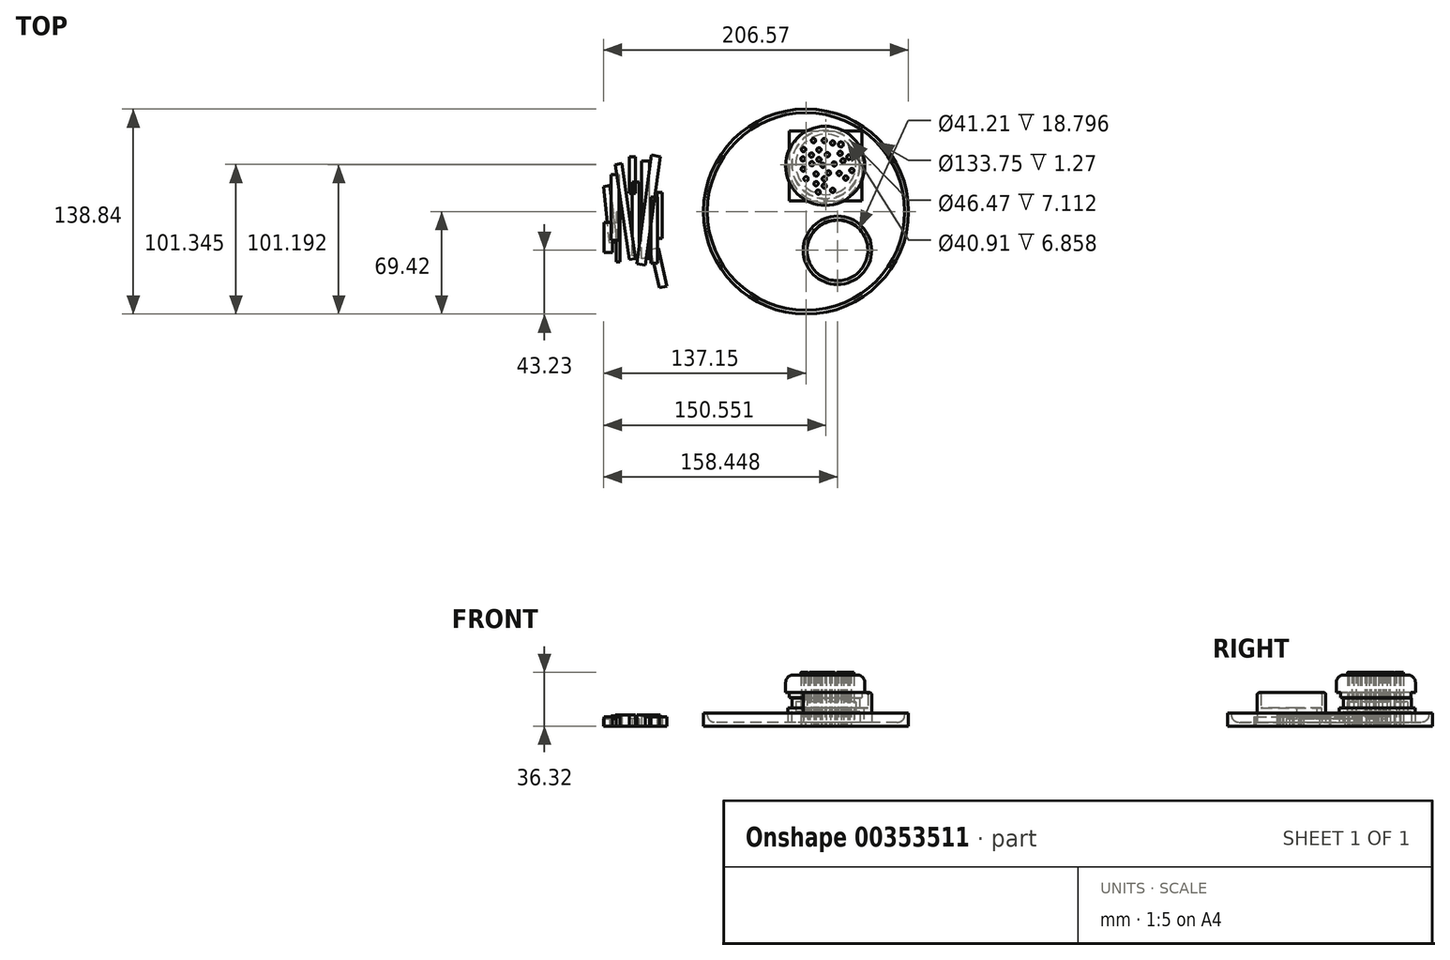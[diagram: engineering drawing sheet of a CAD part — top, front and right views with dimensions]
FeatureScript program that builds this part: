
annotation { "Feature Type Name" : "Feature", "Feature Type Description" : "" }
export const myFeature = defineFeature(function(context is Context, id is Id, definition is map)
    precondition{}
    {
        {
            var Q0;
            Q0=qCreatedBy(makeId("Top.planeOp"),FACE);
            var sketch = newSketch(context, id + "F0", { "sketchPlane" : qUnion([Q0])});
            skCircle(sketch, "E0", {"center": v(0, 0) * mm, "radius": 69.42 * mm});
            skSolve(sketch);
        }
        {
            var Q0;
            Q0=makeQuery(id+"F0.imprint","IMPRINT",FACE,{"disambiguationData":[TD([[makeQuery(id+"F0.imprint","IMPRINT",EDGE,{"derivedFrom":sQuery(id+"F0.wireOp",EDGE,"E0")}),1.0]])]});
            extrude(context, id + "F1", {"entities" : qUnion([Q0]), "depth" : 8.9 * mm});
        }
        {
            var Q0;
            Q0=makeQuery(id+"F1.opExtrude","CAP_FACE",FACE,{"disambiguationData":[OSD([sQuery(id+"F0.wireOp",EDGE,"E0")])],"isStart":false});
            shell(context, id + "F2", {"entities" : qUnion([Q0]), "thickness" : 2.54 * mm});
        }
        {
            var Q0;
            {var subQ0=sQuery(id+"F0.wireOp",EDGE,"E0");Q0=makeQuery(id+"F2.opShell","OFFSET_FACE",FACE,{"disambiguationData":[OSD([subQ0]),TDD([makeQuery(id+"F1.opExtrude","CAP_FACE",FACE,{"disambiguationData":[OSD([subQ0])],"isStart":true})])]});}
            fillet(context, id + "F3", {"entities" : qUnion([Q0]), "radius" : 5.08 * mm, "tangentPropagation" : true, "allowEdgeOverflow" : false});
        }
        {
            var Q0;
            Q0=qCreatedBy(makeId("Top.planeOp"),FACE);
            var sketch = newSketch(context, id + "F4", { "sketchPlane" : qUnion([Q0])});
            skCircle(sketch, "E1", {"center": v(13.4, 31.77) * mm, "radius": 25.78 * mm});
            skSolve(sketch);
        }
        {
            var Q0;
            Q0 = qSketchRegion(id + "F4", true);
            extrude(context, id + "F5", {"entities" : qUnion([Q0]), "operationType" : NewBodyOperationType.ADD, "depth" : 12.2 * mm});
        }
        {
            var Q0;
            Q0=qCreatedBy(makeId("Top.planeOp"),FACE);
            var sketch = newSketch(context, id + "F6", { "sketchPlane" : qUnion([Q0])});
            skCircle(sketch, "E2", {"center": v(13.4, 31.93) * mm, "radius": 23 * mm});
            skSolve(sketch);
        }
        {
            var Q0;
            Q0 = qSketchRegion(id + "F6", true);
            extrude(context, id + "F7", {"entities" : qUnion([Q0]), "operationType" : NewBodyOperationType.ADD, "depth" : 19.05 * mm});
        }
        {
            var Q0;
            Q0=qCreatedBy(makeId("Top.planeOp"),FACE);
            var sketch = newSketch(context, id + "F8", { "sketchPlane" : qUnion([Q0])});
            skLineSegment(sketch, "E3.bottom", {"start": v(-11.22, 54.68) * mm, "end": v(37.7, 54.68) * mm});
            skLineSegment(sketch, "E3.top", {"start": v(-11.22, 7.2) * mm, "end": v(37.7, 7.2) * mm});
            skLineSegment(sketch, "E3.left", {"start": v(-11.22, 54.68) * mm, "end": v(-11.22, 7.2) * mm});
            skLineSegment(sketch, "E3.right", {"start": v(37.7, 54.68) * mm, "end": v(37.7, 7.2) * mm});
            skSolve(sketch);
        }
        {
            var Q0;
            Q0 = qSketchRegion(id + "F8", true);
            extrude(context, id + "F9", {"entities" : qUnion([Q0]), "depth" : 22.86 * mm, "hasSecondDirection" : true, "secondDirectionOppositeDirection" : false, "secondDirectionDepth" : 19.3 * mm});
        }
        {
            var Q0;
            Q0=qCreatedBy(makeId("Top.planeOp"),FACE);
            var sketch = newSketch(context, id + "F10", { "sketchPlane" : qUnion([Q0])});
            skCircle(sketch, "E4", {"center": v(13, 30.94) * mm, "radius": 26.8 * mm});
            skSolve(sketch);
        }
        {
            var Q0;
            Q0 = qSketchRegion(id + "F10", true);
            extrude(context, id + "F11", {"entities" : qUnion([Q0]), "depth" : 34.54 * mm, "hasSecondDirection" : true, "secondDirectionOppositeDirection" : false, "secondDirectionDepth" : 22.6 * mm});
        }
        {
            var Q0;
            Q0=makeQuery(id+"F11.opExtrude","CAP_FACE",FACE,{"disambiguationData":[OSD([sQuery(id+"F10.wireOp",EDGE,"E4")])],"isStart":false});
            fillet(context, id + "F12", {"entities" : qUnion([Q0]), "radius" : 5.08 * mm, "tangentPropagation" : true, "allowEdgeOverflow" : false});
        }
        {
            var Q0;
            Q0=qCreatedBy(makeId("Top.planeOp"),FACE);
            var sketch = newSketch(context, id + "F13", { "sketchPlane" : qUnion([Q0])});
            skCircle(sketch, "E5", {"center": v(0, 22.16) * mm, "radius": 1.47 * mm});
            skCircle(sketch, "E6", {"center": v(12.38, 22.16) * mm, "radius": 1.44 * mm});
            skCircle(sketch, "E7.1.0", {"center": v(6.76, 25.4) * mm, "radius": 1.44 * mm});
            skCircle(sketch, "E7.2.0", {"center": v(6.76, 18.92) * mm, "radius": 1.44 * mm});
            skPoint(sketch, "E7.center", {"position": v(8.63, 22.16) * mm});
            skCircle(sketch, "E8.1.0", {"center": v(11.4, 31.35) * mm, "radius": 1.44 * mm});
            skCircle(sketch, "E8.2.0", {"center": v(3.93, 32.4) * mm, "radius": 1.44 * mm});
            skPoint(sketch, "E8.center", {"position": v(7.37, 29.72) * mm});
            skCircle(sketch, "E9.1.0", {"center": v(19.1, 32.28) * mm, "radius": 1.44 * mm});
            skCircle(sketch, "E9.2.0", {"center": v(14.45, 38.48) * mm, "radius": 1.44 * mm});
            skPoint(sketch, "E9.center", {"position": v(14.99, 34.04) * mm});
            skCircle(sketch, "E10.1.0", {"center": v(15.25, 26.2) * mm, "radius": 1.44 * mm});
            skCircle(sketch, "E10.2.0", {"center": v(22.45, 25.9) * mm, "radius": 1.44 * mm});
            skPoint(sketch, "E10.center", {"position": v(18.93, 28.12) * mm});
            skCircle(sketch, "E11.1.0", {"center": v(-2.09, 35.6) * mm, "radius": 1.44 * mm});
            skCircle(sketch, "E11.2.0", {"center": v(-1.84, 28.79) * mm, "radius": 1.44 * mm});
            skPoint(sketch, "E11.center", {"position": v(0, 32.26) * mm});
            skCircle(sketch, "E12.1.0", {"center": v(8.75, 41.77) * mm, "radius": 1.44 * mm});
            skCircle(sketch, "E12.2.0", {"center": v(8.75, 35.18) * mm, "radius": 1.44 * mm});
            skPoint(sketch, "E12.center", {"position": v(10.65, 38.48) * mm});
            skCircle(sketch, "E13.1.0", {"center": v(3.66, 38.31) * mm, "radius": 1.44 * mm});
            skCircle(sketch, "E13.2.0", {"center": v(-1.57, 41.92) * mm, "radius": 1.44 * mm});
            skPoint(sketch, "E13.center", {"position": v(0, 38.6) * mm});
            skCircle(sketch, "E14.1.0", {"center": v(18.05, 14.36) * mm, "radius": 1.44 * mm});
            skCircle(sketch, "E14.2.0", {"center": v(26.9, 22.7) * mm, "radius": 1.44 * mm});
            skPoint(sketch, "E14.center", {"position": v(20.07, 21.08) * mm});
            skCircle(sketch, "E15.1.0", {"center": v(8.25, 13.24) * mm, "radius": 1.44 * mm});
            skCircle(sketch, "E15.2.0", {"center": v(12.42, 17.37) * mm, "radius": 1.44 * mm});
            skPoint(sketch, "E15.center", {"position": v(9.14, 16.51) * mm});
            skCircle(sketch, "E16.1.0", {"center": v(12.38, 48.07) * mm, "radius": 1.44 * mm});
            skCircle(sketch, "E16.2.0", {"center": v(5.1, 48.07) * mm, "radius": 1.44 * mm});
            skPoint(sketch, "E16.center", {"position": v(8.75, 45.97) * mm});
            skCircle(sketch, "E17.1.0", {"center": v(23.12, 39.32) * mm, "radius": 1.44 * mm});
            skCircle(sketch, "E17.2.0", {"center": v(18.05, 46.4) * mm, "radius": 1.44 * mm});
            skPoint(sketch, "E17.center", {"position": v(18.54, 41.4) * mm});
            skCircle(sketch, "E18.1.0", {"center": v(31.05, 27.84) * mm, "radius": 1.44 * mm});
            skCircle(sketch, "E18.2.0", {"center": v(25.07, 34.32) * mm, "radius": 1.44 * mm});
            skPoint(sketch, "E18.center", {"position": v(26.2, 29.36) * mm});
            skCircle(sketch, "E19", {"center": v(23.6, 45.47) * mm, "radius": 1.68 * mm});
            skCircle(sketch, "E20", {"center": v(29.07, 36.84) * mm, "radius": 1.55 * mm});
            skSolve(sketch);
        }
        {
            var Q0;
            Q0 = qSketchRegion(id + "F13", true);
            extrude(context, id + "F14", {"entities" : qUnion([Q0]), "depth" : 36.32 * mm});
        }
        {
            var Q0;
            Q0=qCreatedBy(makeId("Top.planeOp"),FACE);
            var sketch = newSketch(context, id + "F15", { "sketchPlane" : qUnion([Q0])});
            skCircle(sketch, "E21", {"center": v(21.3, -26.2) * mm, "radius": 23.15 * mm});
            skSolve(sketch);
        }
        {
            var Q0;
            Q0 = qSketchRegion(id + "F15", true);
            extrude(context, id + "F16", {"entities" : qUnion([Q0]), "operationType" : NewBodyOperationType.ADD, "depth" : 22.6 * mm});
        }
        {
            var Q0;
            Q0=makeQuery(id+"F16.opExtrude","CAP_FACE",FACE,{"disambiguationData":[OSD([sQuery(id+"F15.wireOp",EDGE,"E21")])],"isStart":false});
            shell(context, id + "F17", {"entities" : qUnion([Q0]), "thickness" : 2.54 * mm});
        }
        {
            var Q0;
            Q0=qCreatedBy(makeId("Top.planeOp"),FACE);
            var sketch = newSketch(context, id + "F18", { "sketchPlane" : qUnion([Q0])});
            skCircle(sketch, "E22", {"center": v(21.59, -26.86) * mm, "radius": 21.01 * mm});
            skSolve(sketch);
        }
        {
            var Q0;
            Q0 = qSketchRegion(id + "F18", true);
            extrude(context, id + "F19", {"entities" : qUnion([Q0]), "operationType" : NewBodyOperationType.ADD, "depth" : 12.2 * mm});
        }
        {
            var Q0;
            Q0=makeQuery(id+"F16.opExtrude","CAP_FACE",FACE,{"disambiguationData":[OSD([sQuery(id+"F15.wireOp",EDGE,"E21")])],"isStart":false});
            fillet(context, id + "F20", {"entities" : qUnion([Q0]), "radius" : 1.27 * mm, "tangentPropagation" : true, "allowEdgeOverflow" : false});
        }
        {
            var Q0;
            {var subQ0=sQuery(id+"F0.wireOp",EDGE,"E0");Q0=makeQuery(id+"F2.opShell","OFFSET_FACE",FACE,{"disambiguationData":[OSD([subQ0]),TDD([makeQuery(id+"F1.opExtrude","CAP_FACE",FACE,{"disambiguationData":[OSD([subQ0])],"isStart":true})])]});}
            var sketch = newSketch(context, id + "F21", { "sketchPlane" : qUnion([Q0])});
            skLineSegment(sketch, "E23", {"start": v(-16.66, -51.58) * mm, "end": v(-11.5, -50.47) * mm});
            skLineSegment(sketch, "E24", {"start": v(-11.5, -50.47) * mm, "end": v(-17.03, -24.69) * mm});
            skLineSegment(sketch, "E25", {"start": v(-16.66, -51.58) * mm, "end": v(-22.18, -25.8) * mm});
            skLineSegment(sketch, "E26", {"start": v(-17.03, -24.69) * mm, "end": v(-22.18, -25.8) * mm});
            skLineSegment(sketch, "E27.bottom", {"start": v(-17.7, -35.04) * mm, "end": v(-22.38, -35.04) * mm});
            skLineSegment(sketch, "E27.top", {"start": v(-17.7, 9.94) * mm, "end": v(-22.38, 9.94) * mm});
            skLineSegment(sketch, "E27.left", {"start": v(-17.7, -35.04) * mm, "end": v(-17.7, 9.94) * mm});
            skLineSegment(sketch, "E27.right", {"start": v(-22.38, -35.04) * mm, "end": v(-22.38, 9.94) * mm});
            skLineSegment(sketch, "E28.bottom", {"start": v(-18.01, -18.14) * mm, "end": v(-14.48, -18.14) * mm});
            skLineSegment(sketch, "E28.top", {"start": v(-18.01, 12.94) * mm, "end": v(-14.48, 12.94) * mm});
            skLineSegment(sketch, "E28.left", {"start": v(-18.01, -18.14) * mm, "end": v(-18.01, 12.94) * mm});
            skLineSegment(sketch, "E28.right", {"start": v(-14.48, -18.14) * mm, "end": v(-14.48, 12.94) * mm});
            skLineSegment(sketch, "E29.bottom", {"start": v(-23.27, -31.75) * mm, "end": v(-28.7, -31.75) * mm});
            skLineSegment(sketch, "E29.top", {"start": v(-23.27, 34.38) * mm, "end": v(-28.7, 34.38) * mm});
            skLineSegment(sketch, "E29.left", {"start": v(-23.27, -31.75) * mm, "end": v(-23.27, 34.38) * mm});
            skLineSegment(sketch, "E29.right", {"start": v(-28.7, -31.75) * mm, "end": v(-28.7, 34.38) * mm});
            skLineSegment(sketch, "E30", {"start": v(-31.92, -35.38) * mm, "end": v(-25.96, -36.2) * mm});
            skLineSegment(sketch, "E31", {"start": v(-25.96, -36.2) * mm, "end": v(-15.94, 37.11) * mm});
            skLineSegment(sketch, "E32", {"start": v(-31.92, -35.38) * mm, "end": v(-21.85, 38.21) * mm});
            skLineSegment(sketch, "E33", {"start": v(-21.85, 38.21) * mm, "end": v(-15.94, 37.11) * mm});
            skLineSegment(sketch, "E34.bottom", {"start": v(-30.05, -29.87) * mm, "end": v(-34.83, -29.87) * mm});
            skLineSegment(sketch, "E34.top", {"start": v(-30.05, 19.9) * mm, "end": v(-34.83, 19.9) * mm});
            skLineSegment(sketch, "E34.left", {"start": v(-30.05, -29.87) * mm, "end": v(-30.05, 19.9) * mm});
            skLineSegment(sketch, "E34.right", {"start": v(-34.83, -29.87) * mm, "end": v(-34.83, 19.9) * mm});
            skLineSegment(sketch, "E35.bottom", {"start": v(-32.72, 12.42) * mm, "end": v(-36.92, 12.42) * mm});
            skLineSegment(sketch, "E35.top", {"start": v(-32.72, 37.2) * mm, "end": v(-36.92, 37.2) * mm});
            skLineSegment(sketch, "E35.left", {"start": v(-32.72, 12.42) * mm, "end": v(-32.72, 37.2) * mm});
            skLineSegment(sketch, "E35.right", {"start": v(-36.92, 12.42) * mm, "end": v(-36.92, 37.2) * mm});
            skLineSegment(sketch, "E36.bottom", {"start": v(-49.16, 24.98) * mm, "end": v(-43.84, 24.98) * mm});
            skLineSegment(sketch, "E36.top", {"start": v(-49.16, -19.55) * mm, "end": v(-43.84, -19.55) * mm});
            skLineSegment(sketch, "E36.left", {"start": v(-49.16, 24.98) * mm, "end": v(-49.16, -19.55) * mm});
            skLineSegment(sketch, "E36.right", {"start": v(-43.84, 24.98) * mm, "end": v(-43.84, -19.55) * mm});
            skLineSegment(sketch, "E37.bottom", {"start": v(-54, -7.22) * mm, "end": v(-48.26, -7.22) * mm});
            skLineSegment(sketch, "E37.top", {"start": v(-54, -27.67) * mm, "end": v(-48.26, -27.67) * mm});
            skLineSegment(sketch, "E37.left", {"start": v(-54, -7.22) * mm, "end": v(-54, -27.67) * mm});
            skLineSegment(sketch, "E37.right", {"start": v(-48.26, -7.22) * mm, "end": v(-48.26, -27.67) * mm});
            skLineSegment(sketch, "E38", {"start": v(-54.35, 16.89) * mm, "end": v(-50.02, 17.6) * mm});
            skLineSegment(sketch, "E39", {"start": v(-50.02, 17.6) * mm, "end": v(-45.46, -20.8) * mm});
            skLineSegment(sketch, "E40", {"start": v(-45.46, -20.8) * mm, "end": v(-50.32, -21.38) * mm});
            skLineSegment(sketch, "E41", {"start": v(-50.32, -21.38) * mm, "end": v(-54.35, 16.89) * mm});
            skLineSegment(sketch, "E42", {"start": v(-46.26, 31.64) * mm, "end": v(-41.9, 32.61) * mm});
            skLineSegment(sketch, "E43", {"start": v(-41.9, 32.61) * mm, "end": v(-32.57, -31.75) * mm});
            skLineSegment(sketch, "E44", {"start": v(-32.57, -31.75) * mm, "end": v(-36.92, -32.38) * mm});
            skLineSegment(sketch, "E45", {"start": v(-36.92, -32.38) * mm, "end": v(-46.26, 31.64) * mm});
            skLineSegment(sketch, "E46", {"start": v(-45.87, -33.94) * mm, "end": v(-43.17, -33.94) * mm});
            skLineSegment(sketch, "E47", {"start": v(-43.17, -33.94) * mm, "end": v(-43.17, 0) * mm});
            skLineSegment(sketch, "E48", {"start": v(-43.17, 0) * mm, "end": v(-45.85, -0.4) * mm});
            skLineSegment(sketch, "E49", {"start": v(-45.85, -0.4) * mm, "end": v(-45.87, -33.94) * mm});
            skSolve(sketch);
        }
        {
            var Q0;
            {var subQ5=sQuery(id+"F21.wireOp",EDGE,"E23");Q0=makeQuery(id+"F21.imprint","IMPRINT",FACE,{"disambiguationData":[TD([[makeQuery(id+"F21.imprint","IMPRINT",EDGE,{"derivedFrom":subQ5}),1.0]])]});}
            var Q1;
            {var subQ0=sQuery(id+"F21.wireOp",EDGE,"E26");var subQ1=sQuery(id+"F21.wireOp",EDGE,"E25");var subQ2=makeQuery(id+"F21.imprint","INTERSECT",VERTEX,{"derivedFrom":[subQ1,subQ0]});Q1=makeQuery(id+"F21.imprint","IMPRINT",FACE,{"disambiguationData":[TD([[makeQuery(id+"F21.imprint","IMPRINT",EDGE,{"disambiguationData":[TD([[subQ2,1.0]])],"derivedFrom":subQ1}),-1.0]])]});}
            extrude(context, id + "F22", {"entities" : qUnion([Q0, Q1]), "depth" : 6.35 * mm});
        }
        {
            var Q0;
            {var subQ8=sQuery(id+"F21.wireOp",EDGE,"E25");var subQ10=sQuery(id+"F21.wireOp",EDGE,"E26");var subQ11=makeQuery(id+"F21.imprint","INTERSECT",VERTEX,{"derivedFrom":[subQ8,subQ10]});Q0=makeQuery(id+"F21.imprint","IMPRINT",FACE,{"disambiguationData":[TD([[makeQuery(id+"F21.imprint","IMPRINT",EDGE,{"disambiguationData":[TD([[subQ11,1.0]])],"derivedFrom":subQ8}),1.0]])]});}
            var Q1;
            {var subQ0=sQuery(id+"F21.wireOp",EDGE,"E26");var subQ1=sQuery(id+"F21.wireOp",EDGE,"E25");var subQ2=makeQuery(id+"F21.imprint","INTERSECT",VERTEX,{"derivedFrom":[subQ1,subQ0]});Q1=makeQuery(id+"F21.imprint","IMPRINT",FACE,{"disambiguationData":[TD([[makeQuery(id+"F21.imprint","IMPRINT",EDGE,{"disambiguationData":[TD([[subQ2,1.0]])],"derivedFrom":subQ1}),-1.0]])]});}
            var Q2;
            {var subQ0=sQuery(id+"F21.wireOp",EDGE,"E27.left");var subQ1=sQuery(id+"F21.wireOp",EDGE,"E27.top");var subQ2=makeQuery(id+"F21.imprint","INTERSECT",VERTEX,{"derivedFrom":[subQ1,subQ0]});Q2=makeQuery(id+"F21.imprint","IMPRINT",FACE,{"disambiguationData":[TD([[makeQuery(id+"F21.imprint","IMPRINT",EDGE,{"disambiguationData":[TD([[subQ2,-1.0]])],"derivedFrom":subQ1}),1.0]])]});}
            var Q3;
            {var subQ0=sQuery(id+"F21.wireOp",EDGE,"E27.right");var subQ1=sQuery(id+"F21.wireOp",EDGE,"E27.top");var subQ2=makeQuery(id+"F21.imprint","INTERSECT",VERTEX,{"derivedFrom":[subQ1,subQ0]});Q3=makeQuery(id+"F21.imprint","IMPRINT",FACE,{"disambiguationData":[TD([[makeQuery(id+"F21.imprint","IMPRINT",EDGE,{"disambiguationData":[TD([[subQ2,1.0]])],"derivedFrom":subQ1}),1.0]])]});}
            extrude(context, id + "F23", {"entities" : qUnion([Q0, Q1, Q2, Q3]), "depth" : 7.62 * mm});
        }
        {
            var Q0;
            {var subQ4=sQuery(id+"F21.wireOp",EDGE,"E28.top");Q0=makeQuery(id+"F21.imprint","IMPRINT",FACE,{"disambiguationData":[TD([[makeQuery(id+"F21.imprint","IMPRINT",EDGE,{"derivedFrom":subQ4}),-1.0]])]});}
            var Q1;
            {var subQ0=sQuery(id+"F21.wireOp",EDGE,"E27.left");var subQ1=sQuery(id+"F21.wireOp",EDGE,"E27.top");var subQ2=makeQuery(id+"F21.imprint","INTERSECT",VERTEX,{"derivedFrom":[subQ1,subQ0]});Q1=makeQuery(id+"F21.imprint","IMPRINT",FACE,{"disambiguationData":[TD([[makeQuery(id+"F21.imprint","IMPRINT",EDGE,{"disambiguationData":[TD([[subQ2,-1.0]])],"derivedFrom":subQ1}),1.0]])]});}
            extrude(context, id + "F24", {"entities" : qUnion([Q0, Q1]), "depth" : 5.08 * mm});
        }
        {
            var Q0;
            {var subQ1=sQuery(id+"F21.wireOp",EDGE,"E30");Q0=makeQuery(id+"F21.imprint","IMPRINT",FACE,{"disambiguationData":[TD([[makeQuery(id+"F21.imprint","IMPRINT",EDGE,{"derivedFrom":subQ1}),1.0]])]});}
            var Q1;
            {var subQ1=sQuery(id+"F21.wireOp",EDGE,"E29.bottom");var subQ7=sQuery(id+"F21.wireOp",EDGE,"E29.right");var subQ8=makeQuery(id+"F21.imprint","INTERSECT",VERTEX,{"derivedFrom":[subQ1,subQ7]});Q1=makeQuery(id+"F21.imprint","IMPRINT",FACE,{"disambiguationData":[TD([[makeQuery(id+"F21.imprint","IMPRINT",EDGE,{"disambiguationData":[TD([[subQ8,1.0]])],"derivedFrom":subQ1}),-1.0]])]});}
            var Q2;
            {var subQ10=sQuery(id+"F21.wireOp",EDGE,"E33");Q2=makeQuery(id+"F21.imprint","IMPRINT",FACE,{"disambiguationData":[TD([[makeQuery(id+"F21.imprint","IMPRINT",EDGE,{"derivedFrom":subQ10}),-1.0]])]});}
            var Q3;
            {var subQ0=sQuery(id+"F21.wireOp",EDGE,"E27.right");var subQ1=sQuery(id+"F21.wireOp",EDGE,"E27.top");var subQ2=makeQuery(id+"F21.imprint","INTERSECT",VERTEX,{"derivedFrom":[subQ1,subQ0]});Q3=makeQuery(id+"F21.imprint","IMPRINT",FACE,{"disambiguationData":[TD([[makeQuery(id+"F21.imprint","IMPRINT",EDGE,{"disambiguationData":[TD([[subQ2,1.0]])],"derivedFrom":subQ1}),1.0]])]});}
            var Q4;
            {var subQ0=sQuery(id+"F21.wireOp",EDGE,"E34.bottom");var subQ1=sQuery(id+"F21.wireOp",EDGE,"E32");var subQ2=makeQuery(id+"F21.imprint","INTERSECT",VERTEX,{"derivedFrom":[subQ1,subQ0]});Q4=makeQuery(id+"F21.imprint","IMPRINT",FACE,{"disambiguationData":[TD([[makeQuery(id+"F21.imprint","IMPRINT",EDGE,{"disambiguationData":[TD([[subQ2,-1.0]])],"derivedFrom":subQ1}),-1.0]])]});}
            extrude(context, id + "F25", {"entities" : qUnion([Q0, Q1, Q2, Q3, Q4]), "depth" : 7.62 * mm});
        }
        {
            var Q0;
            {var subQ0=sQuery(id+"F21.wireOp",EDGE,"E29.left");var subQ1=sQuery(id+"F21.wireOp",EDGE,"E29.bottom");var subQ2=makeQuery(id+"F21.imprint","INTERSECT",VERTEX,{"derivedFrom":[subQ1,subQ0]});Q0=makeQuery(id+"F21.imprint","IMPRINT",FACE,{"disambiguationData":[TD([[makeQuery(id+"F21.imprint","IMPRINT",EDGE,{"disambiguationData":[TD([[subQ2,-1.0]])],"derivedFrom":subQ1}),-1.0]])]});}
            var Q1;
            {var subQ0=sQuery(id+"F21.wireOp",EDGE,"E29.top");Q1=makeQuery(id+"F21.imprint","IMPRINT",FACE,{"disambiguationData":[TD([[makeQuery(id+"F21.imprint","IMPRINT",EDGE,{"derivedFrom":subQ0}),1.0]])]});}
            var Q2;
            {var subQ1=sQuery(id+"F21.wireOp",EDGE,"E29.bottom");var subQ7=sQuery(id+"F21.wireOp",EDGE,"E29.right");var subQ8=makeQuery(id+"F21.imprint","INTERSECT",VERTEX,{"derivedFrom":[subQ1,subQ7]});Q2=makeQuery(id+"F21.imprint","IMPRINT",FACE,{"disambiguationData":[TD([[makeQuery(id+"F21.imprint","IMPRINT",EDGE,{"disambiguationData":[TD([[subQ8,1.0]])],"derivedFrom":subQ1}),-1.0]])]});}
            extrude(context, id + "F26", {"entities" : qUnion([Q0, Q1, Q2]), "depth" : 6.35 * mm});
        }
        {
            var Q0;
            {var subQ0=sQuery(id+"F21.wireOp",EDGE,"E34.bottom");var subQ1=sQuery(id+"F21.wireOp",EDGE,"E32");var subQ2=makeQuery(id+"F21.imprint","INTERSECT",VERTEX,{"derivedFrom":[subQ1,subQ0]});Q0=makeQuery(id+"F21.imprint","IMPRINT",FACE,{"disambiguationData":[TD([[makeQuery(id+"F21.imprint","IMPRINT",EDGE,{"disambiguationData":[TD([[subQ2,-1.0]])],"derivedFrom":subQ1}),-1.0]])]});}
            var Q1;
            {var subQ0=sQuery(id+"F21.wireOp",EDGE,"E34.right");var subQ1=sQuery(id+"F21.wireOp",EDGE,"E34.bottom");var subQ2=makeQuery(id+"F21.imprint","INTERSECT",VERTEX,{"derivedFrom":[subQ1,subQ0]});Q1=makeQuery(id+"F21.imprint","IMPRINT",FACE,{"disambiguationData":[TD([[makeQuery(id+"F21.imprint","IMPRINT",EDGE,{"disambiguationData":[TD([[subQ2,1.0]])],"derivedFrom":subQ1}),-1.0]])]});}
            var Q2;
            {var subQ5=sQuery(id+"F21.wireOp",EDGE,"E32");var subQ7=sQuery(id+"F21.wireOp",EDGE,"E34.bottom");var subQ8=makeQuery(id+"F21.imprint","INTERSECT",VERTEX,{"derivedFrom":[subQ5,subQ7]});Q2=makeQuery(id+"F21.imprint","IMPRINT",FACE,{"disambiguationData":[TD([[makeQuery(id+"F21.imprint","IMPRINT",EDGE,{"disambiguationData":[TD([[subQ8,-1.0]])],"derivedFrom":subQ5}),1.0]])]});}
            var Q3;
            {var subQ0=sQuery(id+"F21.wireOp",EDGE,"E34.right");var subQ1=sQuery(id+"F21.wireOp",EDGE,"E34.top");var subQ2=makeQuery(id+"F21.imprint","INTERSECT",VERTEX,{"derivedFrom":[subQ1,subQ0]});Q3=makeQuery(id+"F21.imprint","IMPRINT",FACE,{"disambiguationData":[TD([[makeQuery(id+"F21.imprint","IMPRINT",EDGE,{"disambiguationData":[TD([[subQ2,1.0]])],"derivedFrom":subQ1}),1.0]])]});}
            extrude(context, id + "F27", {"entities" : qUnion([Q0, Q1, Q2, Q3]), "depth" : 5.08 * mm});
        }
        {
            var Q0;
            {var subQ0=sQuery(id+"F21.wireOp",EDGE,"E34.right");var subQ1=sQuery(id+"F21.wireOp",EDGE,"E34.top");var subQ2=makeQuery(id+"F21.imprint","INTERSECT",VERTEX,{"derivedFrom":[subQ1,subQ0]});Q0=makeQuery(id+"F21.imprint","IMPRINT",FACE,{"disambiguationData":[TD([[makeQuery(id+"F21.imprint","IMPRINT",EDGE,{"disambiguationData":[TD([[subQ2,1.0]])],"derivedFrom":subQ1}),1.0]])]});}
            var Q1;
            {var subQ0=sQuery(id+"F21.wireOp",EDGE,"E35.top");Q1=makeQuery(id+"F21.imprint","IMPRINT",FACE,{"disambiguationData":[TD([[makeQuery(id+"F21.imprint","IMPRINT",EDGE,{"derivedFrom":subQ0}),1.0]])]});}
            extrude(context, id + "F28", {"entities" : qUnion([Q0, Q1]), "depth" : 5.08 * mm});
        }
        {
            var Q0;
            {var subQ6=sQuery(id+"F21.wireOp",EDGE,"E42");Q0=makeQuery(id+"F21.imprint","IMPRINT",FACE,{"disambiguationData":[TD([[makeQuery(id+"F21.imprint","IMPRINT",EDGE,{"derivedFrom":subQ6}),-1.0]])]});}
            var Q1;
            {var subQ0=sQuery(id+"F21.wireOp",EDGE,"E36.right");var subQ1=sQuery(id+"F21.wireOp",EDGE,"E36.bottom");var subQ2=makeQuery(id+"F21.imprint","INTERSECT",VERTEX,{"derivedFrom":[subQ1,subQ0]});Q1=makeQuery(id+"F21.imprint","IMPRINT",FACE,{"disambiguationData":[TD([[makeQuery(id+"F21.imprint","IMPRINT",EDGE,{"disambiguationData":[TD([[subQ2,1.0]])],"derivedFrom":subQ1}),-1.0]])]});}
            var Q2;
            {var subQ0=sQuery(id+"F21.wireOp",EDGE,"E34.right");var subQ1=sQuery(id+"F21.wireOp",EDGE,"E34.bottom");var subQ2=makeQuery(id+"F21.imprint","INTERSECT",VERTEX,{"derivedFrom":[subQ1,subQ0]});Q2=makeQuery(id+"F21.imprint","IMPRINT",FACE,{"disambiguationData":[TD([[makeQuery(id+"F21.imprint","IMPRINT",EDGE,{"disambiguationData":[TD([[subQ2,1.0]])],"derivedFrom":subQ1}),-1.0]])]});}
            extrude(context, id + "F29", {"entities" : qUnion([Q0, Q1, Q2]), "depth" : 7.62 * mm});
        }
        {
            var Q0;
            {var subQ0=sQuery(id+"F21.wireOp",EDGE,"E36.right");var subQ1=sQuery(id+"F21.wireOp",EDGE,"E36.bottom");var subQ2=makeQuery(id+"F21.imprint","INTERSECT",VERTEX,{"derivedFrom":[subQ1,subQ0]});Q0=makeQuery(id+"F21.imprint","IMPRINT",FACE,{"disambiguationData":[TD([[makeQuery(id+"F21.imprint","IMPRINT",EDGE,{"disambiguationData":[TD([[subQ2,1.0]])],"derivedFrom":subQ1}),-1.0]])]});}
            var Q1;
            {var subQ1=sQuery(id+"F21.wireOp",EDGE,"E36.left");var subQ5=sQuery(id+"F21.wireOp",EDGE,"E36.bottom");var subQ6=makeQuery(id+"F21.imprint","INTERSECT",VERTEX,{"derivedFrom":[subQ5,subQ1]});Q1=makeQuery(id+"F21.imprint","IMPRINT",FACE,{"disambiguationData":[TD([[makeQuery(id+"F21.imprint","IMPRINT",EDGE,{"disambiguationData":[TD([[subQ6,-1.0]])],"derivedFrom":subQ5}),-1.0]])]});}
            var Q2;
            {var subQ0=sQuery(id+"F21.wireOp",EDGE,"E37.right");var subQ5=sQuery(id+"F21.wireOp",EDGE,"E36.top");var subQ6=makeQuery(id+"F21.imprint","INTERSECT",VERTEX,{"derivedFrom":[subQ5,subQ0]});Q2=makeQuery(id+"F21.imprint","IMPRINT",FACE,{"disambiguationData":[TD([[makeQuery(id+"F21.imprint","IMPRINT",EDGE,{"disambiguationData":[TD([[subQ6,-1.0]])],"derivedFrom":subQ5}),1.0]])]});}
            var Q3;
            {var subQ0=sQuery(id+"F21.wireOp",EDGE,"E36.left");var subQ1=sQuery(id+"F21.wireOp",EDGE,"E36.top");var subQ2=makeQuery(id+"F21.imprint","INTERSECT",VERTEX,{"derivedFrom":[subQ1,subQ0]});Q3=makeQuery(id+"F21.imprint","IMPRINT",FACE,{"disambiguationData":[TD([[makeQuery(id+"F21.imprint","IMPRINT",EDGE,{"disambiguationData":[TD([[subQ2,-1.0]])],"derivedFrom":subQ1}),1.0]])]});}
            var Q4;
            {var subQ1=sQuery(id+"F21.wireOp",EDGE,"E36.top");var subQ7=sQuery(id+"F21.wireOp",EDGE,"E36.right");var subQ9=makeQuery(id+"F21.imprint","INTERSECT",VERTEX,{"derivedFrom":[subQ1,subQ7]});Q4=makeQuery(id+"F21.imprint","IMPRINT",FACE,{"disambiguationData":[TD([[makeQuery(id+"F21.imprint","IMPRINT",EDGE,{"disambiguationData":[TD([[subQ9,1.0]])],"derivedFrom":subQ1}),1.0]])]});}
            var Q5;
            {var subQ0=sQuery(id+"F21.wireOp",EDGE,"E49");var subQ1=sQuery(id+"F21.wireOp",EDGE,"E36.top");var subQ2=makeQuery(id+"F21.imprint","INTERSECT",VERTEX,{"derivedFrom":[subQ1,subQ0]});Q5=makeQuery(id+"F21.imprint","IMPRINT",FACE,{"disambiguationData":[TD([[makeQuery(id+"F21.imprint","IMPRINT",EDGE,{"disambiguationData":[TD([[subQ2,-1.0]])],"derivedFrom":subQ1}),1.0]])]});}
            extrude(context, id + "F30", {"entities" : qUnion([Q0, Q1, Q2, Q3, Q4, Q5]), "depth" : 6.86 * mm});
        }
        {
            var Q0;
            {var subQ11=sQuery(id+"F21.wireOp",EDGE,"E46");Q0=makeQuery(id+"F21.imprint","IMPRINT",FACE,{"disambiguationData":[TD([[makeQuery(id+"F21.imprint","IMPRINT",EDGE,{"derivedFrom":subQ11}),1.0]])]});}
            var Q1;
            {var subQ1=sQuery(id+"F21.wireOp",EDGE,"E36.top");var subQ7=sQuery(id+"F21.wireOp",EDGE,"E36.right");var subQ9=makeQuery(id+"F21.imprint","INTERSECT",VERTEX,{"derivedFrom":[subQ1,subQ7]});Q1=makeQuery(id+"F21.imprint","IMPRINT",FACE,{"disambiguationData":[TD([[makeQuery(id+"F21.imprint","IMPRINT",EDGE,{"disambiguationData":[TD([[subQ9,1.0]])],"derivedFrom":subQ1}),1.0]])]});}
            var Q2;
            {var subQ0=sQuery(id+"F21.wireOp",EDGE,"E49");var subQ1=sQuery(id+"F21.wireOp",EDGE,"E36.top");var subQ2=makeQuery(id+"F21.imprint","INTERSECT",VERTEX,{"derivedFrom":[subQ1,subQ0]});Q2=makeQuery(id+"F21.imprint","IMPRINT",FACE,{"disambiguationData":[TD([[makeQuery(id+"F21.imprint","IMPRINT",EDGE,{"disambiguationData":[TD([[subQ2,-1.0]])],"derivedFrom":subQ1}),-1.0]])]});}
            var Q3;
            {var subQ0=sQuery(id+"F21.wireOp",EDGE,"E49");var subQ1=sQuery(id+"F21.wireOp",EDGE,"E36.top");var subQ2=makeQuery(id+"F21.imprint","INTERSECT",VERTEX,{"derivedFrom":[subQ1,subQ0]});Q3=makeQuery(id+"F21.imprint","IMPRINT",FACE,{"disambiguationData":[TD([[makeQuery(id+"F21.imprint","IMPRINT",EDGE,{"disambiguationData":[TD([[subQ2,-1.0]])],"derivedFrom":subQ1}),1.0]])]});}
            extrude(context, id + "F31", {"entities" : qUnion([Q0, Q1, Q2, Q3]), "depth" : 6.35 * mm});
        }
        {
            var Q0;
            {var subQ1=sQuery(id+"F21.wireOp",EDGE,"E38");Q0=makeQuery(id+"F21.imprint","IMPRINT",FACE,{"disambiguationData":[TD([[makeQuery(id+"F21.imprint","IMPRINT",EDGE,{"derivedFrom":subQ1}),-1.0]])]});}
            var Q1;
            {var subQ0=sQuery(id+"F21.wireOp",EDGE,"E37.right");var subQ5=sQuery(id+"F21.wireOp",EDGE,"E36.top");var subQ6=makeQuery(id+"F21.imprint","INTERSECT",VERTEX,{"derivedFrom":[subQ5,subQ0]});Q1=makeQuery(id+"F21.imprint","IMPRINT",FACE,{"disambiguationData":[TD([[makeQuery(id+"F21.imprint","IMPRINT",EDGE,{"disambiguationData":[TD([[subQ6,-1.0]])],"derivedFrom":subQ5}),1.0]])]});}
            var Q2;
            {var subQ0=sQuery(id+"F21.wireOp",EDGE,"E36.left");var subQ1=sQuery(id+"F21.wireOp",EDGE,"E36.top");var subQ2=makeQuery(id+"F21.imprint","INTERSECT",VERTEX,{"derivedFrom":[subQ1,subQ0]});Q2=makeQuery(id+"F21.imprint","IMPRINT",FACE,{"disambiguationData":[TD([[makeQuery(id+"F21.imprint","IMPRINT",EDGE,{"disambiguationData":[TD([[subQ2,-1.0]])],"derivedFrom":subQ1}),1.0]])]});}
            var Q3;
            {var subQ1=sQuery(id+"F21.wireOp",EDGE,"E36.top");var subQ6=sQuery(id+"F21.wireOp",EDGE,"E36.left");var subQ10=makeQuery(id+"F21.imprint","INTERSECT",VERTEX,{"derivedFrom":[subQ1,subQ6]});Q3=makeQuery(id+"F21.imprint","IMPRINT",FACE,{"disambiguationData":[TD([[makeQuery(id+"F21.imprint","IMPRINT",EDGE,{"disambiguationData":[TD([[subQ10,-1.0]])],"derivedFrom":subQ1}),-1.0]])]});}
            var Q4;
            {var subQ0=sQuery(id+"F21.wireOp",EDGE,"E37.right");var subQ1=sQuery(id+"F21.wireOp",EDGE,"E36.top");var subQ2=makeQuery(id+"F21.imprint","INTERSECT",VERTEX,{"derivedFrom":[subQ1,subQ0]});Q4=makeQuery(id+"F21.imprint","IMPRINT",FACE,{"disambiguationData":[TD([[makeQuery(id+"F21.imprint","IMPRINT",EDGE,{"disambiguationData":[TD([[subQ2,-1.0]])],"derivedFrom":subQ1}),-1.0]])]});}
            var Q5;
            {var subQ0=sQuery(id+"F21.wireOp",EDGE,"E49");var subQ1=sQuery(id+"F21.wireOp",EDGE,"E36.top");var subQ2=makeQuery(id+"F21.imprint","INTERSECT",VERTEX,{"derivedFrom":[subQ1,subQ0]});Q5=makeQuery(id+"F21.imprint","IMPRINT",FACE,{"disambiguationData":[TD([[makeQuery(id+"F21.imprint","IMPRINT",EDGE,{"disambiguationData":[TD([[subQ2,-1.0]])],"derivedFrom":subQ1}),-1.0]])]});}
            var Q6;
            {var subQ0=sQuery(id+"F21.wireOp",EDGE,"E49");var subQ1=sQuery(id+"F21.wireOp",EDGE,"E36.top");var subQ2=makeQuery(id+"F21.imprint","INTERSECT",VERTEX,{"derivedFrom":[subQ1,subQ0]});Q6=makeQuery(id+"F21.imprint","IMPRINT",FACE,{"disambiguationData":[TD([[makeQuery(id+"F21.imprint","IMPRINT",EDGE,{"disambiguationData":[TD([[subQ2,-1.0]])],"derivedFrom":subQ1}),1.0]])]});}
            extrude(context, id + "F32", {"entities" : qUnion([Q0, Q1, Q2, Q3, Q4, Q5, Q6]), "depth" : 5.08 * mm});
        }
        {
            var Q0;
            {var subQ1=sQuery(id+"F21.wireOp",EDGE,"E37.top");Q0=makeQuery(id+"F21.imprint","IMPRINT",FACE,{"disambiguationData":[TD([[makeQuery(id+"F21.imprint","IMPRINT",EDGE,{"derivedFrom":subQ1}),1.0]])]});}
            var Q1;
            {var subQ1=sQuery(id+"F21.wireOp",EDGE,"E36.top");var subQ6=sQuery(id+"F21.wireOp",EDGE,"E36.left");var subQ10=makeQuery(id+"F21.imprint","INTERSECT",VERTEX,{"derivedFrom":[subQ1,subQ6]});Q1=makeQuery(id+"F21.imprint","IMPRINT",FACE,{"disambiguationData":[TD([[makeQuery(id+"F21.imprint","IMPRINT",EDGE,{"disambiguationData":[TD([[subQ10,-1.0]])],"derivedFrom":subQ1}),-1.0]])]});}
            var Q2;
            {var subQ0=sQuery(id+"F21.wireOp",EDGE,"E36.left");var subQ1=sQuery(id+"F21.wireOp",EDGE,"E36.top");var subQ2=makeQuery(id+"F21.imprint","INTERSECT",VERTEX,{"derivedFrom":[subQ1,subQ0]});Q2=makeQuery(id+"F21.imprint","IMPRINT",FACE,{"disambiguationData":[TD([[makeQuery(id+"F21.imprint","IMPRINT",EDGE,{"disambiguationData":[TD([[subQ2,-1.0]])],"derivedFrom":subQ1}),1.0]])]});}
            extrude(context, id + "F33", {"entities" : qUnion([Q0, Q1, Q2]), "depth" : 6.35 * mm});
        }
        {
            var Q0;
            Q0=makeQuery(id+"F24.opExtrude","SWEPT_BODY",BODY,{"disambiguationData":[OSD([sQuery(id+"F21.wireOp",EDGE,"E28.bottom"),sQuery(id+"F21.wireOp",EDGE,"E28.top"),sQuery(id+"F21.wireOp",EDGE,"E28.left"),sQuery(id+"F21.wireOp",EDGE,"E28.right")])]});
            var Q1;
            Q1=makeQuery(id+"F23.opExtrude","SWEPT_BODY",BODY,{"disambiguationData":[OSD([sQuery(id+"F21.wireOp",EDGE,"E27.bottom"),sQuery(id+"F21.wireOp",EDGE,"E27.top"),sQuery(id+"F21.wireOp",EDGE,"E27.left"),sQuery(id+"F21.wireOp",EDGE,"E27.right")])]});
            var Q2;
            Q2=makeQuery(id+"F22.opExtrude","SWEPT_BODY",BODY,{"disambiguationData":[OSD([sQuery(id+"F21.wireOp",EDGE,"E23"),sQuery(id+"F21.wireOp",EDGE,"E24"),sQuery(id+"F21.wireOp",EDGE,"E25"),sQuery(id+"F21.wireOp",EDGE,"E26")])]});
            var Q3;
            Q3=makeQuery(id+"F25.opExtrude","SWEPT_BODY",BODY,{"disambiguationData":[OSD([sQuery(id+"F21.wireOp",EDGE,"E30"),sQuery(id+"F21.wireOp",EDGE,"E31"),sQuery(id+"F21.wireOp",EDGE,"E32"),sQuery(id+"F21.wireOp",EDGE,"E33")])]});
            var Q4;
            Q4=makeQuery(id+"F26.opExtrude","SWEPT_BODY",BODY,{"disambiguationData":[OSD([sQuery(id+"F21.wireOp",EDGE,"E29.bottom"),sQuery(id+"F21.wireOp",EDGE,"E29.top"),sQuery(id+"F21.wireOp",EDGE,"E29.left"),sQuery(id+"F21.wireOp",EDGE,"E29.right")])]});
            var Q5;
            Q5=makeQuery(id+"F27.opExtrude","SWEPT_BODY",BODY,{"disambiguationData":[OSD([sQuery(id+"F21.wireOp",EDGE,"E34.bottom"),sQuery(id+"F21.wireOp",EDGE,"E34.top"),sQuery(id+"F21.wireOp",EDGE,"E34.left"),sQuery(id+"F21.wireOp",EDGE,"E34.right")])]});
            var Q6;
            Q6=makeQuery(id+"F28.opExtrude","SWEPT_BODY",BODY,{"disambiguationData":[OSD([sQuery(id+"F21.wireOp",EDGE,"E35.bottom"),sQuery(id+"F21.wireOp",EDGE,"E35.top"),sQuery(id+"F21.wireOp",EDGE,"E35.left"),sQuery(id+"F21.wireOp",EDGE,"E35.right")])]});
            var Q7;
            Q7=makeQuery(id+"F29.opExtrude","SWEPT_BODY",BODY,{"disambiguationData":[OSD([sQuery(id+"F21.wireOp",EDGE,"E42"),sQuery(id+"F21.wireOp",EDGE,"E43"),sQuery(id+"F21.wireOp",EDGE,"E44"),sQuery(id+"F21.wireOp",EDGE,"E45")])]});
            var Q8;
            Q8=makeQuery(id+"F30.opExtrude","SWEPT_BODY",BODY,{"disambiguationData":[OSD([sQuery(id+"F21.wireOp",EDGE,"E36.bottom"),sQuery(id+"F21.wireOp",EDGE,"E36.top"),sQuery(id+"F21.wireOp",EDGE,"E36.left"),sQuery(id+"F21.wireOp",EDGE,"E36.right")])]});
            var Q9;
            Q9=makeQuery(id+"F32.opExtrude","SWEPT_BODY",BODY,{"disambiguationData":[OSD([sQuery(id+"F21.wireOp",EDGE,"E38"),sQuery(id+"F21.wireOp",EDGE,"E39"),sQuery(id+"F21.wireOp",EDGE,"E40"),sQuery(id+"F21.wireOp",EDGE,"E41")])]});
            var Q10;
            Q10=makeQuery(id+"F33.opExtrude","SWEPT_BODY",BODY,{"disambiguationData":[OSD([sQuery(id+"F21.wireOp",EDGE,"E37.bottom"),sQuery(id+"F21.wireOp",EDGE,"E37.top"),sQuery(id+"F21.wireOp",EDGE,"E37.left"),sQuery(id+"F21.wireOp",EDGE,"E37.right")])]});
            var Q11;
            Q11=makeQuery(id+"F31.opExtrude","SWEPT_BODY",BODY,{"disambiguationData":[OSD([sQuery(id+"F21.wireOp",EDGE,"E46"),sQuery(id+"F21.wireOp",EDGE,"E47"),sQuery(id+"F21.wireOp",EDGE,"E48"),sQuery(id+"F21.wireOp",EDGE,"E49")])]});
            transform(context, id + "F34", {"entities" : qUnion([Q0, Q1, Q2, Q3, Q4, Q5, Q6, Q7, Q8, Q9, Q10, Q11]), "transformType" : TransformType.TRANSLATION_3D, "dx" : -82.8 * mm, "dy" : 0 * mm, "dz" : -2.54 * mm, "makeCopy" : false});
        }
    });
